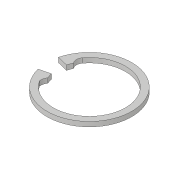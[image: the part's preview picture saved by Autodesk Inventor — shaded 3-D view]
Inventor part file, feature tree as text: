
AUTODESK INVENTOR PART (.ipt)
format: ipt  version: 2019 (Build 230136000, 136)  size: 105,984 bytes
history: native  units: in
note: dims shown in document units (in); Inventor stores cm internally (conversion verified against a paired STEP export)
features: extrude x1, sketch x1
ambient origin geometry x8: Origin, YZ Plane, XZ Plane, XY Plane, X Axis, Y Axis, Z Axis, Center Point
bodies: Solid1 (feature_tree)
feature tree (2):
  extrude  "Extrusion1"  Depth=0.0591in
  sketch  "Sketch1"  dims[d0=1.063in d1=0.9055in d2=0.0962in d3=0.0962in d4=0.7874in d5=0.0687in d6=0.0687in d7=0.0591in d8=0.0in]
